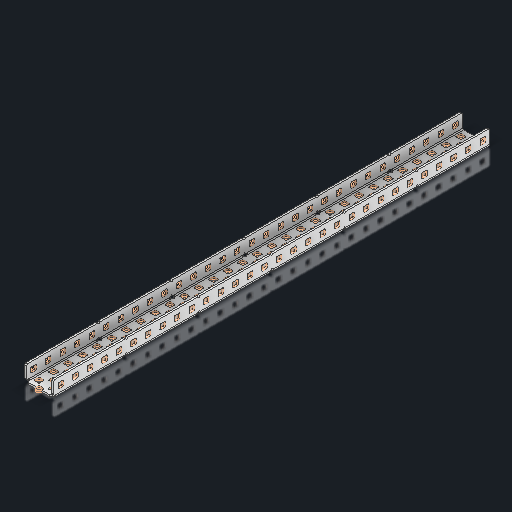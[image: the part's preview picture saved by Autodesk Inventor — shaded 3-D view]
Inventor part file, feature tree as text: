
AUTODESK INVENTOR PART (.ipt)
format: ipt  version: 2023.2 (Build 272271030, 271C)  size: 2,490,880 bytes
history: native  units: in
note: dims shown in document units (in); Inventor stores cm internally (conversion verified against a paired STEP export)
features: other x306, sketch x10, sheet_metal_op x1
ambient origin geometry x8: Origin, YZ Plane, XZ Plane, XY Plane, X Axis, Y Axis, Z Axis, Center Point
bodies: Solid1 (feature_tree)
feature tree (317):
  other  "Alu C 1x2x1x30.ipt"
  other  "Solid1::Alu C 1x2x1x30.ipt"
  other  "TaggingFeature1"
  sketch  "Sketch1"  dims[d0=0.3937in]
  sketch  "Sketch2"  dims[d1=0.0625in]
  sketch  "Sketch3"
  sketch  "Sketch7"
  other  "Flange Pattern Sketch"
  sketch  "Sketch8"
  sketch  "Sketch9"
  sheet_metal_op  "Body Pattern Sketch"
  sketch  "Sketch15"
  sketch  "Sketch16"
  other  "Arc Length"
  sketch  "Sketch13"
  sketch  "Sketch14"
  other  "Flange Pattern Plane"
  other  "Srf1"
  other  "Srf2"
  other  "Srf3"
  other  "Srf4"
  other  "Srf5"
  other  "Srf6"
  other  "Srf7"
  other  "Srf8"
  other  "Srf9"
  other  "Srf10"
  other  "Srf11"
  other  "Srf12"
  other  "Srf13"
  other  "Srf14"
  other  "Srf15"
  other  "Srf16"
  other  "Srf17"
  other  "Srf18"
  other  "Srf19"
  other  "Srf20"
  other  "Srf21"
  other  "Srf22"
  other  "Srf23"
  other  "Srf24"
  other  "Srf25"
  other  "Srf26"
  other  "Srf27"
  other  "Srf28"
  other  "Srf29"
  other  "Srf30"
  other  "Srf31"
  other  "Srf32"
  other  "Srf33"
  other  "Srf34"
  other  "Srf35"
  other  "Srf36"
  other  "Srf37"
  other  "Srf38"
  other  "Srf39"
  other  "Srf40"
  other  "Srf41"
  other  "Srf42"
  other  "Srf43"
  other  "Srf44"
  other  "Srf45"
  other  "Srf46"
  other  "Srf47"
  other  "Srf48"
  other  "Srf49"
  other  "Srf50"
  other  "Srf51"
  other  "Srf52"
  other  "Srf53"
  other  "Srf54"
  other  "Srf55"
  other  "Srf56"
  other  "Srf57"
  other  "Srf58"
  other  "Srf59"
  other  "Srf60"
  other  "Srf61"
  other  "Srf62"
  other  "Srf63"
  other  "Srf64"
  other  "Srf65"
  other  "Srf66"
  other  "Srf67"
  other  "Srf68"
  other  "Srf69"
  other  "Srf70"
  other  "Srf71"
  other  "Srf72"
  other  "Srf73"
  other  "Srf74"
  other  "Srf75"
  other  "Srf76"
  other  "Srf77"
  other  "Srf78"
  other  "Srf79"
  other  "Srf80"
  other  "Srf81"
  other  "Srf82"
  other  "Srf83"
  other  "Srf84"
  other  "Srf85"
  other  "Srf86"
  other  "Srf87"
  other  "Srf88"
  other  "Srf89"
  other  "Srf90"
  other  "Srf91"
  other  "Srf92"
  other  "Srf93"
  other  "Srf94"
  other  "Srf95"
  other  "Srf96"
  other  "Srf97"
  other  "Srf98"
  other  "Srf99"
  other  "Srf100"
  other  "Srf101"
  other  "Srf102"
  other  "Srf103"
  other  "Srf104"
  other  "Srf105"
  other  "Srf106"
  other  "Srf107"
  other  "Srf108"
  other  "Srf109"
  other  "Srf110"
  other  "Srf111"
  other  "Srf112"
  other  "Srf113"
  other  "Srf114"
  other  "Srf115"
  other  "Srf116"
  other  "Srf117"
  other  "Srf118"
  other  "Srf119"
  other  "Srf120"
  other  "Srf121"
  other  "Srf122"
  other  "Srf123"
  other  "Srf124"
  other  "Srf125"
  other  "Srf126"
  other  "Srf127"
  other  "Srf128"
  other  "Srf129"
  other  "Srf130"
  other  "Srf131"
  other  "Srf132"
  other  "Srf133"
  other  "Srf134"
  other  "Srf135"
  other  "Srf136"
  other  "Srf137"
  other  "Srf138"
  other  "Srf139"
  other  "Srf140"
  other  "Srf141"
  other  "Srf142"
  other  "Srf143"
  other  "Srf144"
  other  "Srf145"
  other  "Srf146"
  other  "Srf147"
  other  "Srf148"
  other  "Srf149"
  other  "Srf150"
  other  "Srf1::Derived"
  other  "Srf2::Derived"
  other  "Srf823::Derived"
  other  "Srf824::Derived"
  other  "Srf825::Derived"
  other  "Srf826::Derived"
  other  "Srf827::Derived"
  other  "Srf828::Derived"
  other  "Srf829::Derived"
  other  "Srf922::Derived"
  other  "Srf923::Derived"
  other  "Srf924::Derived"
  other  "Srf925::Derived"
  other  "Srf926::Derived"
  other  "Srf1143::Derived"
  other  "Srf1144::Derived"
  other  "Srf1145::Derived"
  other  "Srf1146::Derived"
  other  "Srf1147::Derived"
  other  "Srf1148::Derived"
  other  "Srf1149::Derived"
  other  "Srf1150::Derived"
  other  "Srf1151::Derived"
  other  "Srf1152::Derived"
  other  "Srf1153::Derived"
  other  "Srf1154::Derived"
  other  "Srf1155::Derived"
  other  "Srf1156::Derived"
  other  "Srf1157::Derived"
  other  "Srf1158::Derived"
  other  "Srf1159::Derived"
  other  "Srf1160::Derived"
  other  "Srf1161::Derived"
  other  "Srf1162::Derived"
  other  "Srf1163::Derived"
  other  "Srf1164::Derived"
  other  "Srf1165::Derived"
  other  "Srf1166::Derived"
  other  "Srf1167::Derived"
  other  "Srf1168::Derived"
  other  "Srf1169::Derived"
  other  "Srf1170::Derived"
  other  "Srf1171::Derived"
  other  "Srf1172::Derived"
  other  "Srf1173::Derived"
  other  "Srf1174::Derived"
  other  "Srf1175::Derived"
  other  "Srf1176::Derived"
  other  "Srf1177::Derived"
  other  "Srf1178::Derived"
  other  "Srf1179::Derived"
  other  "Srf1180::Derived"
  other  "Srf1181::Derived"
  other  "Srf1182::Derived"
  other  "Srf1183::Derived"
  other  "Srf1184::Derived"
  other  "Srf1185::Derived"
  other  "Srf1186::Derived"
  other  "Srf1187::Derived"
  other  "Srf1188::Derived"
  other  "Srf91::Derived"
  other  "Srf92::Derived"
  other  "Srf856::Derived"
  other  "Srf857::Derived"
  other  "Srf858::Derived"
  other  "Srf859::Derived"
  other  "Srf860::Derived"
  other  "Srf861::Derived"
  other  "Srf862::Derived"
  other  "Srf959::Derived"
  other  "Srf960::Derived"
  other  "Srf961::Derived"
  other  "Srf962::Derived"
  other  "Srf963::Derived"
  other  "Srf1199::Derived"
  other  "Srf1200::Derived"
  other  "Srf1201::Derived"
  other  "Srf1202::Derived"
  other  "Srf1203::Derived"
  other  "Srf1204::Derived"
  other  "Srf1205::Derived"
  other  "Srf1206::Derived"
  other  "Srf1207::Derived"
  other  "Srf1208::Derived"
  other  "Srf1209::Derived"
  other  "Srf1210::Derived"
  other  "Srf1211::Derived"
  other  "Srf1212::Derived"
  other  "Srf1213::Derived"
  other  "Srf1214::Derived"
  other  "Srf1215::Derived"
  other  "Srf1216::Derived"
  other  "Srf1217::Derived"
  other  "Srf1218::Derived"
  other  "Srf1219::Derived"
  other  "Srf1220::Derived"
  other  "Srf1221::Derived"
  other  "Srf1222::Derived"
  other  "Srf1223::Derived"
  other  "Srf1224::Derived"
  other  "Srf1225::Derived"
  other  "Srf1226::Derived"
  other  "Srf1227::Derived"
  other  "Srf1228::Derived"
  other  "Srf1229::Derived"
  other  "Srf1230::Derived"
  other  "Srf1231::Derived"
  other  "Srf1232::Derived"
  other  "Srf1233::Derived"
  other  "Srf1234::Derived"
  other  "Srf1235::Derived"
  other  "Srf1236::Derived"
  other  "Srf1237::Derived"
  other  "Srf1238::Derived"
  other  "Srf1239::Derived"
  other  "Srf1240::Derived"
  other  "Srf1241::Derived"
  other  "Srf1242::Derived"
  other  "Srf1243::Derived"
  other  "Srf1244::Derived"
  other  "Srf786::Derived"
  other  "Srf889::Derived"
  other  "Srf890::Derived"
  other  "Srf891::Derived"
  other  "Srf892::Derived"
  other  "Srf893::Derived"
  other  "Srf894::Derived"
  other  "Srf895::Derived"
  other  "Srf896::Derived"
  other  "Srf996::Derived"
  other  "Srf997::Derived"
  other  "Srf998::Derived"
  other  "Srf999::Derived"
  other  "Srf1000::Derived"
  other  "Srf1255::Derived"
  other  "Srf1256::Derived"
  other  "Srf1257::Derived"
  other  "Srf1258::Derived"
  other  "Srf1259::Derived"
  other  "Srf1260::Derived"
  other  "Srf1261::Derived"
  other  "Srf1262::Derived"
  other  "Srf1263::Derived"
  other  "Srf1264::Derived"
  other  "Srf1265::Derived"
  other  "Srf1266::Derived"
  other  "Srf1267::Derived"
  other  "Srf1268::Derived"
  other  "Srf1269::Derived"
  other  "Srf1270::Derived"
